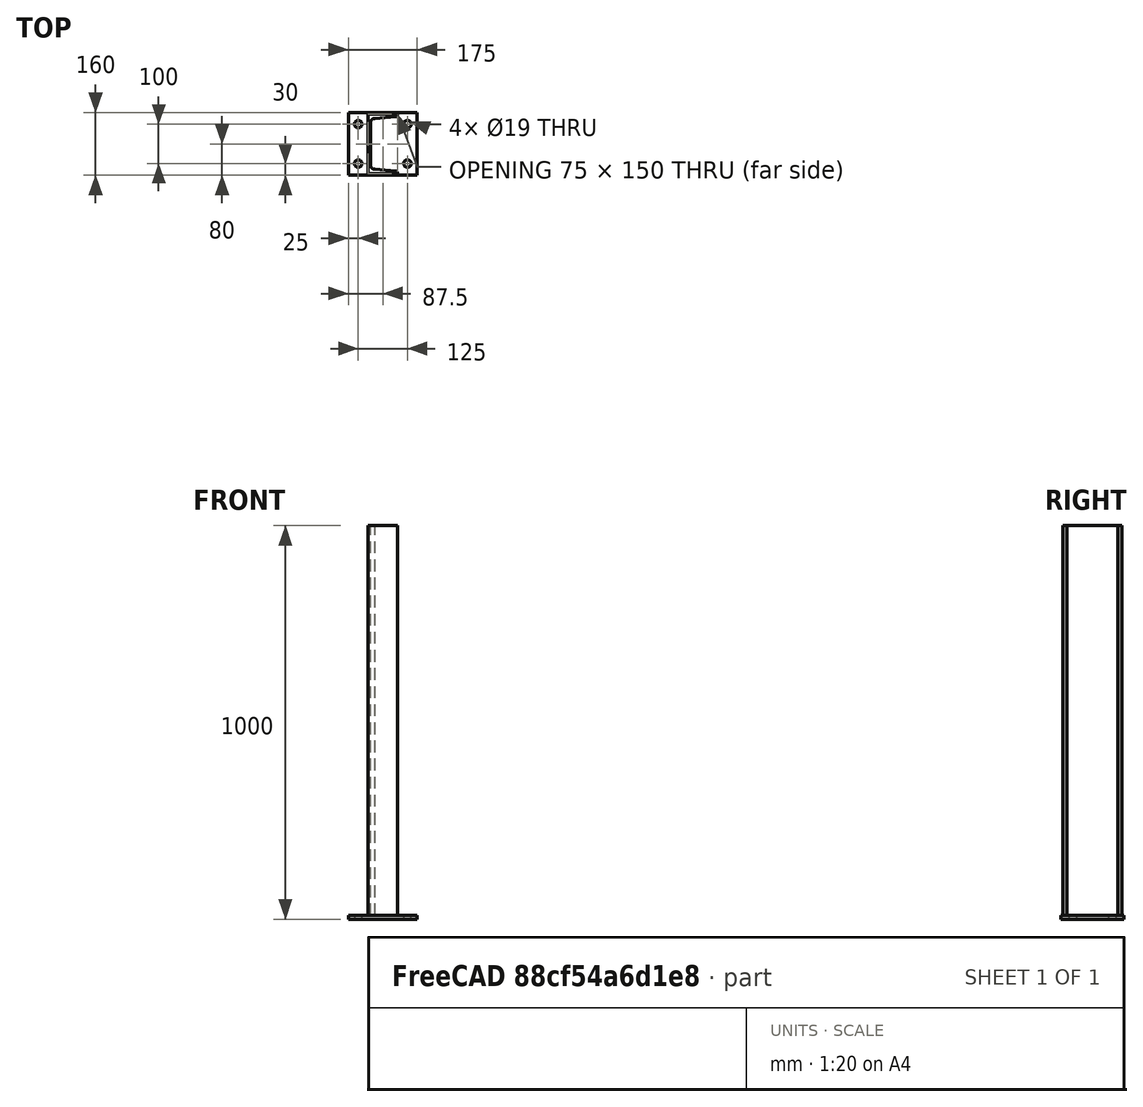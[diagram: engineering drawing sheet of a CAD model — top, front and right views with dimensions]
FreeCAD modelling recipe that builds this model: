
FCSTD DOCUMENT  (FreeCAD 0.21R30492 (Git))
Label: 03_Pst_C
License: All rights reserved
LicenseURL: http://en.wikipedia.org/wiki/All_rights_reserved
objects: Part::FeaturePython×2, Part::Extrusion×1, Part::MultiFuse×1
note: 4 computed .brp shape members not serialized (recipe doc carries the construction recipe); baked Part::Feature solids carry a one-line shape summary decoded from their .brp

FEATURE [Part::FeaturePython] BasePlate  # WARN: FeaturePython — macro-defined, semantics opaque (R4)
  B = 175
  D = 19
  H = 160
  b1 = 25
  h1 = 30
  sface = 0
FEATURE [Part::Extrusion] Extrude
  Base = -> BasePlate
  Dir = (0,0,1)
  DirMode = 2
  FaceMakerClass = Part::FaceMakerBullseye
  LengthFwd = 10
  LengthRev = 0
  Solid = true
  Symmetric = false
FEATURE [Part::FeaturePython] Channel  # WARN: FeaturePython — macro-defined, semantics opaque (R4)
  B = 75
  H = 150
  L = 1000
  Solid = true
  g0 = 7.85
  mass = 16.9049
  size = 3
  standard = SS
FEATURE [Part::MultiFuse] Fusion  label="PostC"
  Shapes = -> [Extrude,Channel]
